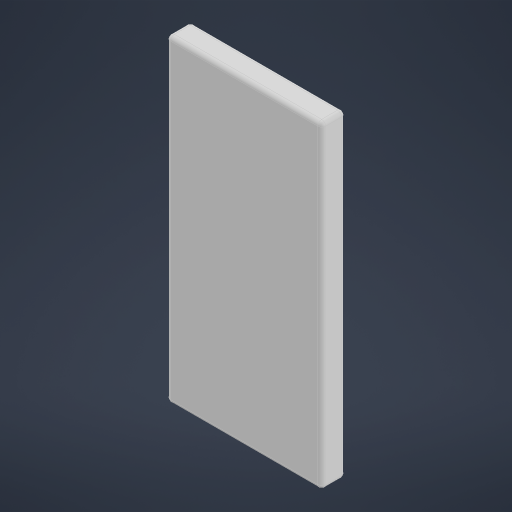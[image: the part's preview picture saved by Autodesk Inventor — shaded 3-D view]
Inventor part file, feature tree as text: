
AUTODESK INVENTOR PART (.ipt)
format: ipt  version: 2023.2 (Build 272271000, 271)  size: 285,696 bytes
history: native  units: mm
features: sketch x1
ambient origin geometry x8: Origin, YZ Plane, XZ Plane, XY Plane, X Axis, Y Axis, Z Axis, Center Point
bodies: Body1 (feature_tree)
feature tree (1):
  sketch  "Sketch1"  dims[d228=78.0mm d229=160.0mm d230=12.0mm d231=0.0mm d232=2.0mm d9=0.5mm d10=0.872665mm d11=0.5mm d12=0.872665mm d13=0.5mm d14=0.872665mm d27=0.5mm d28=0.872665mm d29=0.5mm d30=0.872665mm d88=0.5mm d89=0.872665mm d90=0.5mm d91=0.872665mm d116=0.5mm d117=0.872665mm d118=0.5mm d119=0.872665mm d154=0.5mm d155=0.872665mm d156=0.5mm d157=0.872665mm d181=0.5mm d182=0.872665mm d183=0.5mm d184=0.872665mm d221=0.5mm d222=0.872665mm d223=0.5mm d224=0.872665mm]
